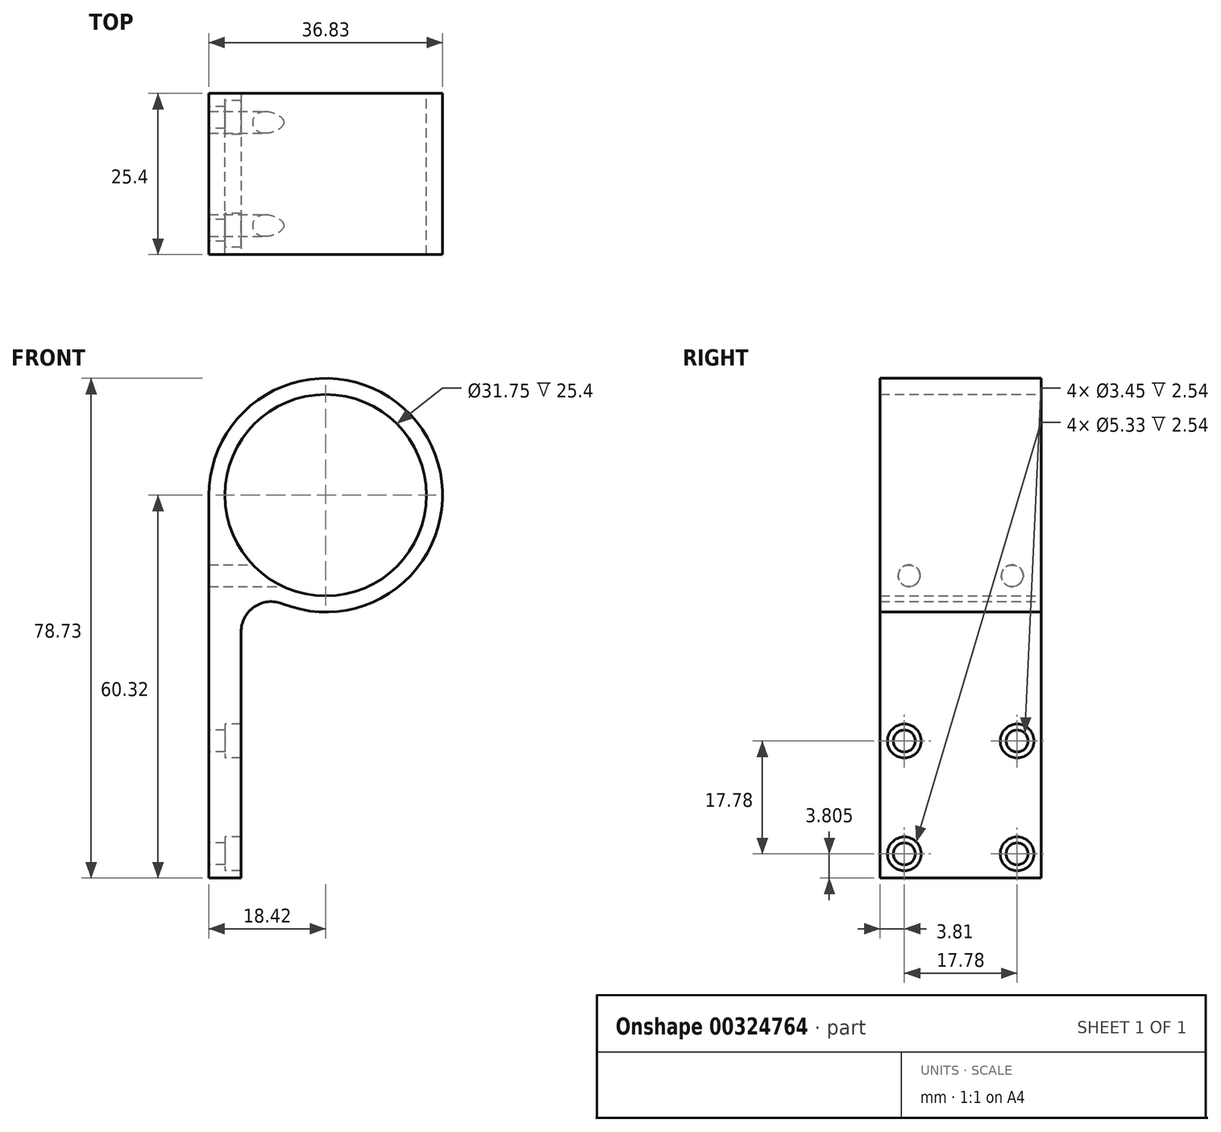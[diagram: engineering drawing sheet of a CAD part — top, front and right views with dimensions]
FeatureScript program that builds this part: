
annotation { "Feature Type Name" : "Feature", "Feature Type Description" : "" }
export const myFeature = defineFeature(function(context is Context, id is Id, definition is map)
    precondition{}
    {
        {
            var Q0;
            Q0=qCreatedBy(makeId("Front.planeOp"),FACE);
            var sketch = newSketch(context, id + "F0", { "sketchPlane" : qUnion([Q0])});
            skArc(sketch, "E0", {"start": v(-13.33, -12.7) * mm, "mid": v(17.1, 6.84) * mm, "end": v(-18.41, 0) * mm});
            skCircle(sketch, "E1", {"center": v(0, 0) * mm, "radius": 15.88 * mm});
            skLineSegment(sketch, "E2", {"start": v(-18.41, 0) * mm, "end": v(-18.41, -60.33) * mm});
            skLineSegment(sketch, "E3", {"start": v(-18.41, -60.33) * mm, "end": v(-13.33, -60.33) * mm});
            skLineSegment(sketch, "E4", {"start": v(-13.33, -60.33) * mm, "end": v(-13.33, -12.7) * mm});
            skSolve(sketch);
        }
        {
            var Q0;
            Q0=makeQuery(id+"F0.imprint","IMPRINT",FACE,{"disambiguationData":[TD([[makeQuery(id+"F0.imprint","IMPRINT",EDGE,{"derivedFrom":sQuery(id+"F0.wireOp",EDGE,"E0")}),1.0]])]});
            extrude(context, id + "F1", {"entities" : qUnion([Q0]), "depth" : 25.4 * mm, "offsetDistance" : 25.4 * mm});
        }
        {
            var Q0;
            Q0=makeQuery(id+"F1.opExtrude","SWEPT_EDGE",EDGE,{"disambiguationData":[OSD([sQuery(id+"F0.wireOp",EDGE,"E0"),sQuery(id+"F0.wireOp",EDGE,"E4")])]});
            fillet(context, id + "F2", {"entities" : qUnion([Q0]), "tangentPropagation" : true, "radius" : 4.76 * mm, "defaultsChanged" : true, "vertexSettings" : [], "allowEdgeOverflow" : false});
        }
        {
            var Q0;
            Q0=makeQuery(id+"F1.opExtrude","SWEPT_FACE",FACE,{"disambiguationData":[OSD([sQuery(id+"F0.wireOp",EDGE,"E2")])]});
            var sketch = newSketch(context, id + "F3", { "sketchPlane" : qUnion([Q0])});
            skPoint(sketch, "E5", {"position": v(4.57, -12.7) * mm});
            skPoint(sketch, "E6", {"position": v(20.83, -12.7) * mm});
            skSolve(sketch);
        }
        {
            var Q0;
            Q0=sQuery(id+"F3.wireOp",VERTEX,"E5");
            var Q1;
            Q1=sQuery(id+"F3.wireOp",VERTEX,"E6");
            var Q2;
            Q2=makeQuery(id+"F1.opExtrude","SWEPT_BODY",BODY,{"disambiguationData":[OSD([sQuery(id+"F0.wireOp",EDGE,"E0"),sQuery(id+"F0.wireOp",EDGE,"E1"),sQuery(id+"F0.wireOp",EDGE,"E2"),sQuery(id+"F0.wireOp",EDGE,"E3"),sQuery(id+"F0.wireOp",EDGE,"E4")])]});
            hole(context, id + "F4", {"style" : HoleStyle.SIMPLE, "endStyle" : HoleEndStyle.BLIND, "holeDiameter" : 3.45 * mm, "majorDiameter" : 6.35 * mm, "holeDepth" : 12.7 * mm, "tappedDepth" : 12.7 * mm, "tapClearance" : 3, "locations" : qUnion([Q0, Q1]), "scope" : qUnion([Q2])});
        }
        {
            var Q0;
            Q0=makeQuery(id+"F1.opExtrude","SWEPT_FACE",FACE,{"disambiguationData":[OSD([sQuery(id+"F0.wireOp",EDGE,"E4")])]});
            var sketch = newSketch(context, id + "F5", { "sketchPlane" : qUnion([Q0])});
            skPoint(sketch, "E7", {"position": v(-21.59, -56.52) * mm});
            skPoint(sketch, "E8", {"position": v(-3.81, -56.52) * mm});
            skPoint(sketch, "E9", {"position": v(-3.81, -38.74) * mm});
            skPoint(sketch, "E10", {"position": v(-21.6, -38.74) * mm});
            skSolve(sketch);
        }
        {
            var Q0;
            Q0=sQuery(id+"F5.wireOp",VERTEX,"E10");
            var Q1;
            Q1=sQuery(id+"F5.wireOp",VERTEX,"E9");
            var Q2;
            Q2=sQuery(id+"F5.wireOp",VERTEX,"E7");
            var Q3;
            Q3=sQuery(id+"F5.wireOp",VERTEX,"E8");
            var Q4;
            Q4=makeQuery(id+"F1.opExtrude","SWEPT_BODY",BODY,{"disambiguationData":[OSD([sQuery(id+"F0.wireOp",EDGE,"E0"),sQuery(id+"F0.wireOp",EDGE,"E1"),sQuery(id+"F0.wireOp",EDGE,"E2"),sQuery(id+"F0.wireOp",EDGE,"E3"),sQuery(id+"F0.wireOp",EDGE,"E4")])]});
            hole(context, id + "F6", {"style" : HoleStyle.C_BORE, "endStyle" : HoleEndStyle.THROUGH, "holeDiameter" : 3.45 * mm, "cBoreDiameter" : 5.33 * mm, "cBoreDepth" : 2.54 * mm, "majorDiameter" : 6.35 * mm, "tappedDepth" : 12.7 * mm, "tapClearance" : 3, "locations" : qUnion([Q0, Q1, Q2, Q3]), "scope" : qUnion([Q4])});
        }
    });
